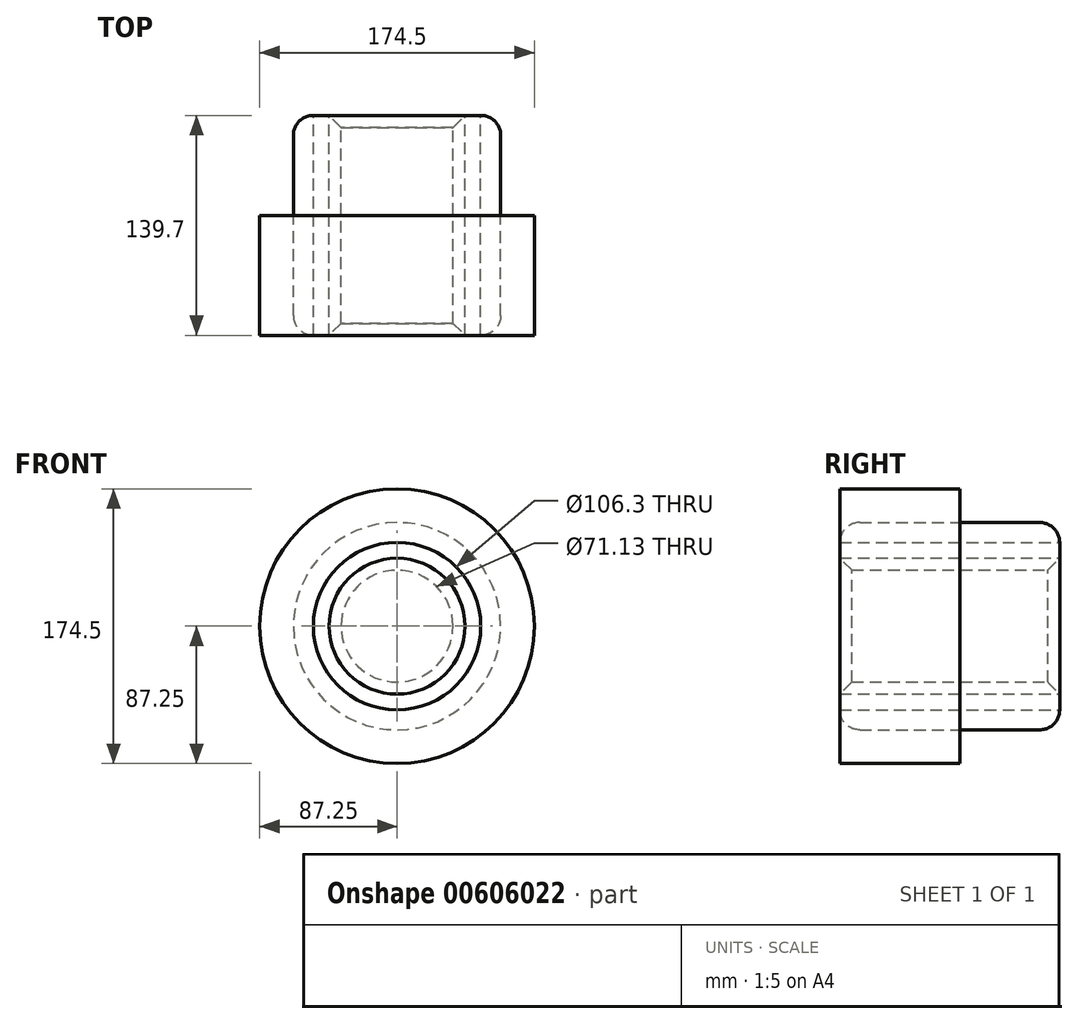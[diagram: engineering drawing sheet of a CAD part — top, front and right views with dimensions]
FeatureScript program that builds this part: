
annotation { "Feature Type Name" : "Feature", "Feature Type Description" : "" }
export const myFeature = defineFeature(function(context is Context, id is Id, definition is map)
    precondition{}
    {
        {
            var Q0;
            Q0=qCreatedBy(makeId("Front.planeOp"),FACE);
            var sketch = newSketch(context, id + "F0", { "sketchPlane" : qUnion([Q0])});
            skCircle(sketch, "E0", {"center": v(0, 0) * mm, "radius": 65.85 * mm});
            skCircle(sketch, "E1", {"center": v(0, 0) * mm, "radius": 56.16 * mm});
            skCircle(sketch, "E2", {"center": v(0, 0) * mm, "radius": 35.57 * mm});
            skLineSegment(sketch, "E3", {"start": v(-45.87, 47.24) * mm, "end": v(-39.02, 40.4) * mm});
            skLineSegment(sketch, "E4", {"start": v(0, 65.85) * mm, "end": v(0, 56.16) * mm});
            skLineSegment(sketch, "E5", {"start": v(42.68, 50.14) * mm, "end": v(35.8, 43.27) * mm});
            skLineSegment(sketch, "E6", {"start": v(56.16, 0) * mm, "end": v(65.85, 0) * mm});
            skLineSegment(sketch, "E7", {"start": v(-65.85, 0) * mm, "end": v(-56.16, 0) * mm});
            skLineSegment(sketch, "E8", {"start": v(0, -56.16) * mm, "end": v(0, -65.85) * mm});
            skLineSegment(sketch, "E9", {"start": v(-39.6, -39.83) * mm, "end": v(-46.45, -46.68) * mm});
            skLineSegment(sketch, "E10", {"start": v(43.59, -35.41) * mm, "end": v(50.47, -42.3) * mm});
            skSolve(sketch);
        }
        {
            var Q0;
            {var subQ0=sQuery(id+"F0.wireOp",EDGE,"E3");Q0=makeQuery(id+"F0.imprint","IMPRINT",FACE,{"disambiguationData":[TD([[makeQuery(id+"F0.imprint","IMPRINT",EDGE,{"derivedFrom":subQ0}),-1.0]])]});}
            var Q1;
            {var subQ0=sQuery(id+"F0.wireOp",EDGE,"E3");Q1=makeQuery(id+"F0.imprint","IMPRINT",FACE,{"disambiguationData":[TD([[makeQuery(id+"F0.imprint","IMPRINT",EDGE,{"derivedFrom":subQ0}),1.0]])]});}
            var Q2;
            {var subQ0=sQuery(id+"F0.wireOp",EDGE,"E4");Q2=makeQuery(id+"F0.imprint","IMPRINT",FACE,{"disambiguationData":[TD([[makeQuery(id+"F0.imprint","IMPRINT",EDGE,{"derivedFrom":subQ0}),1.0]])]});}
            var Q3;
            {var subQ0=sQuery(id+"F0.wireOp",EDGE,"E5");Q3=makeQuery(id+"F0.imprint","IMPRINT",FACE,{"disambiguationData":[TD([[makeQuery(id+"F0.imprint","IMPRINT",EDGE,{"derivedFrom":subQ0}),1.0]])]});}
            var Q4;
            {var subQ0=sQuery(id+"F0.wireOp",EDGE,"E6");Q4=makeQuery(id+"F0.imprint","IMPRINT",FACE,{"disambiguationData":[TD([[makeQuery(id+"F0.imprint","IMPRINT",EDGE,{"derivedFrom":subQ0}),-1.0]])]});}
            var Q5;
            {var subQ0=sQuery(id+"F0.wireOp",EDGE,"E8");Q5=makeQuery(id+"F0.imprint","IMPRINT",FACE,{"disambiguationData":[TD([[makeQuery(id+"F0.imprint","IMPRINT",EDGE,{"derivedFrom":subQ0}),1.0]])]});}
            var Q6;
            {var subQ0=sQuery(id+"F0.wireOp",EDGE,"E8");Q6=makeQuery(id+"F0.imprint","IMPRINT",FACE,{"disambiguationData":[TD([[makeQuery(id+"F0.imprint","IMPRINT",EDGE,{"derivedFrom":subQ0}),-1.0]])]});}
            var Q7;
            {var subQ0=sQuery(id+"F0.wireOp",EDGE,"E7");Q7=makeQuery(id+"F0.imprint","IMPRINT",FACE,{"disambiguationData":[TD([[makeQuery(id+"F0.imprint","IMPRINT",EDGE,{"derivedFrom":subQ0}),-1.0]])]});}
            var Q8;
            Q8=makeQuery(id+"F0.imprint","IMPRINT",FACE,{"disambiguationData":[TD([[makeQuery(id+"F0.imprint","IMPRINT",EDGE,{"derivedFrom":sQuery(id+"F0.wireOp",EDGE,"E2")}),-1.0]])]});
            extrude(context, id + "F1", {"entities" : qUnion([Q0, Q1, Q2, Q3, Q4, Q5, Q6, Q7, Q8]), "depth" : 76.2 * mm, "offsetDistance" : 25.4 * mm, "hasSecondDirection" : true, "secondDirectionOppositeDirection" : true, "secondDirectionDepth" : 63.5 * mm});
        }
        {
            var Q0;
            Q0=makeQuery(id+"F1.opExtrude","CAP_EDGE",EDGE,{"disambiguationData":[OSD([sQuery(id+"F0.wireOp",EDGE,"E0")])],"isStart":false});
            var Q1;
            Q1=makeQuery(id+"F1.opExtrude","CAP_EDGE",EDGE,{"disambiguationData":[OSD([sQuery(id+"F0.wireOp",EDGE,"E0")])],"isStart":true});
            fillet(context, id + "F2", {"entities" : qUnion([Q0, Q1]), "radius" : 12.7 * mm, "tangentPropagation" : true, "allowEdgeOverflow" : false});
        }
        {
            var Q0;
            Q0=makeQuery(id+"F1.opExtrude","CAP_EDGE",EDGE,{"disambiguationData":[OSD([sQuery(id+"F0.wireOp",EDGE,"E2")])],"isStart":false});
            var Q1;
            Q1=makeQuery(id+"F1.opExtrude","CAP_EDGE",EDGE,{"disambiguationData":[OSD([sQuery(id+"F0.wireOp",EDGE,"E2")])],"isStart":true});
            chamfer(context, id + "F3", {"entities" : qUnion([Q0, Q1]), "width" : 7.62 * mm, "tangentPropagation" : true});
        }
        {
            var Q0;
            Q0=makeQuery(id+"F1.opExtrude","CAP_FACE",FACE,{"disambiguationData":[OSD([sQuery(id+"F0.wireOp",EDGE,"E0"),sQuery(id+"F0.wireOp",EDGE,"E2")])],"isStart":true});
            extrude(context, id + "F4", {"entities" : qUnion([Q0]), "operationType" : NewBodyOperationType.REMOVE, "oppositeDirection" : true, "depth" : 177.8 * mm, "offsetDistance" : 25.4 * mm});
        }
        {
            var Q0;
            Q0=qCreatedBy(makeId("Front.planeOp"),FACE);
            var sketch = newSketch(context, id + "F5", { "sketchPlane" : qUnion([Q0])});
            skCircle(sketch, "E11", {"center": v(0, 0) * mm, "radius": 87.25 * mm});
            skSolve(sketch);
        }
        {
            var Q0;
            Q0=makeQuery(id+"F5.imprint","IMPRINT",FACE,{"disambiguationData":[TD([[makeQuery(id+"F5.imprint","IMPRINT",EDGE,{"derivedFrom":sQuery(id+"F5.wireOp",EDGE,"E11")}),1.0]])]});
            extrude(context, id + "F6", {"entities" : qUnion([Q0]), "depth" : 152.4 * mm, "offsetDistance" : 25.4 * mm});
        }
        {
            var Q0;
            Q0=makeQuery(id+"F6.opExtrude","CAP_FACE",FACE,{"disambiguationData":[OSD([sQuery(id+"F5.wireOp",EDGE,"E11")])],"isStart":false});
            extrude(context, id + "F7", {"entities" : qUnion([Q0]), "operationType" : NewBodyOperationType.REMOVE, "oppositeDirection" : true, "depth" : 76.2 * mm, "offsetDistance" : 25.4 * mm});
        }
        {
            var Q0;
            Q0=qCreatedBy(makeId("Front.planeOp"),FACE);
            var sketch = newSketch(context, id + "F8", { "sketchPlane" : qUnion([Q0])});
            skCircle(sketch, "E12", {"center": v(0, 0) * mm, "radius": 42.4 * mm});
            skSolve(sketch);
        }
        {
            var Q0;
            Q0=sQuery(id+"F8.wireOp",EDGE,"E12");
            extrude(context, id + "F9", {"bodyType" : ToolBodyType.SURFACE, "surfaceEntities" : qUnion([Q0]), "endBound" : BoundingType.SYMMETRIC, "depth" : 76.2 * mm, "offsetDistance" : 25.4 * mm});
        }
    });
